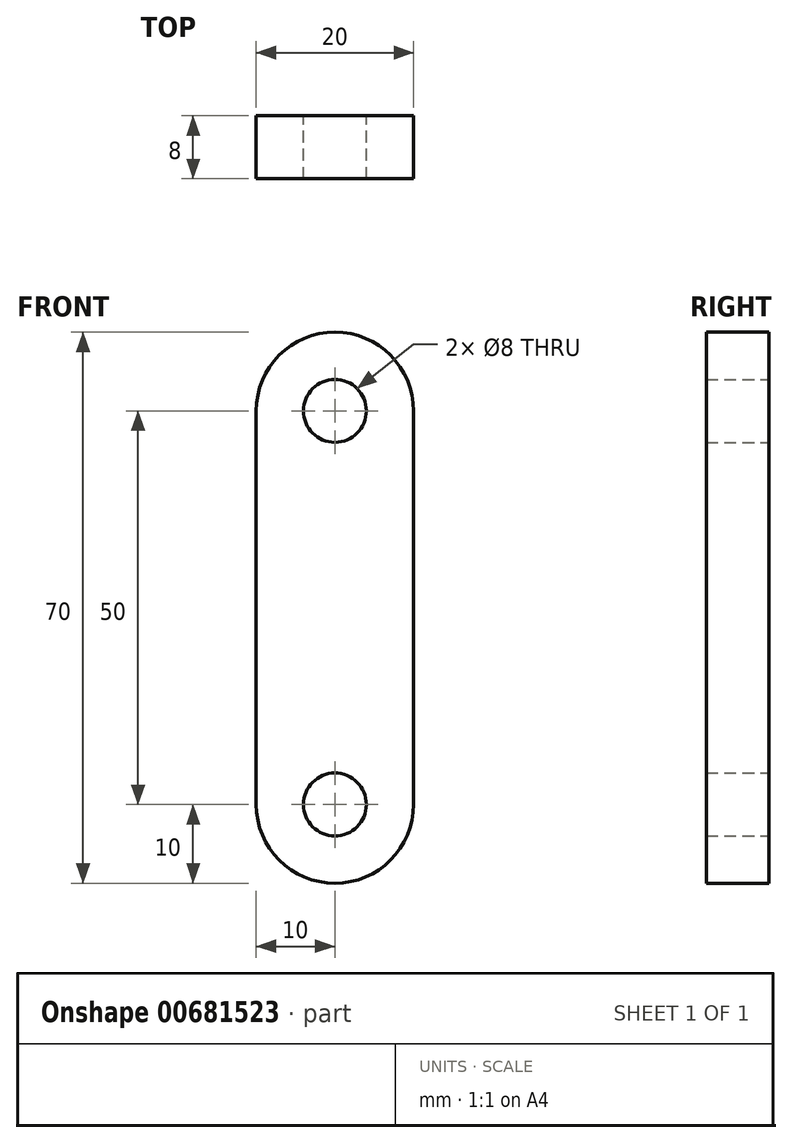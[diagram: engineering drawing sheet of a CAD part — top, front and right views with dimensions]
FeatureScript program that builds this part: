
annotation { "Feature Type Name" : "Feature", "Feature Type Description" : "" }
export const myFeature = defineFeature(function(context is Context, id is Id, definition is map)
    precondition{}
    {
        {
            var Q0;
            Q0=qCreatedBy(makeId("Front.planeOp"),FACE);
            var sketch = newSketch(context, id + "F0", { "sketchPlane" : qUnion([Q0])});
            skCircle(sketch, "E0", {"center": v(0, 0) * mm, "radius": 4 * mm});
            skCircle(sketch, "E1", {"center": v(0, 50) * mm, "radius": 4 * mm});
            skArc(sketch, "E2", {"start": v(-10, 0) * mm, "mid": v(0, -10) * mm, "end": v(10, 0) * mm});
            skArc(sketch, "E3", {"start": v(10, 50) * mm, "mid": v(0, 60) * mm, "end": v(-10, 50) * mm});
            skLineSegment(sketch, "E4", {"start": v(-10, 50) * mm, "end": v(-10, 0) * mm});
            skLineSegment(sketch, "E5", {"start": v(10, 50) * mm, "end": v(10, 0) * mm});
            skSolve(sketch);
        }
        {
            var Q0;
            Q0=makeQuery(id+"F0.imprint","IMPRINT",FACE,{"disambiguationData":[TD([[makeQuery(id+"F0.imprint","IMPRINT",EDGE,{"derivedFrom":sQuery(id+"F0.wireOp",EDGE,"E0")}),-1.0]])]});
            extrude(context, id + "F1", {"entities" : qUnion([Q0]), "endBound" : BoundingType.SYMMETRIC, "depth" : 8 * mm, "offsetDistance" : 25 * mm});
        }
    });
